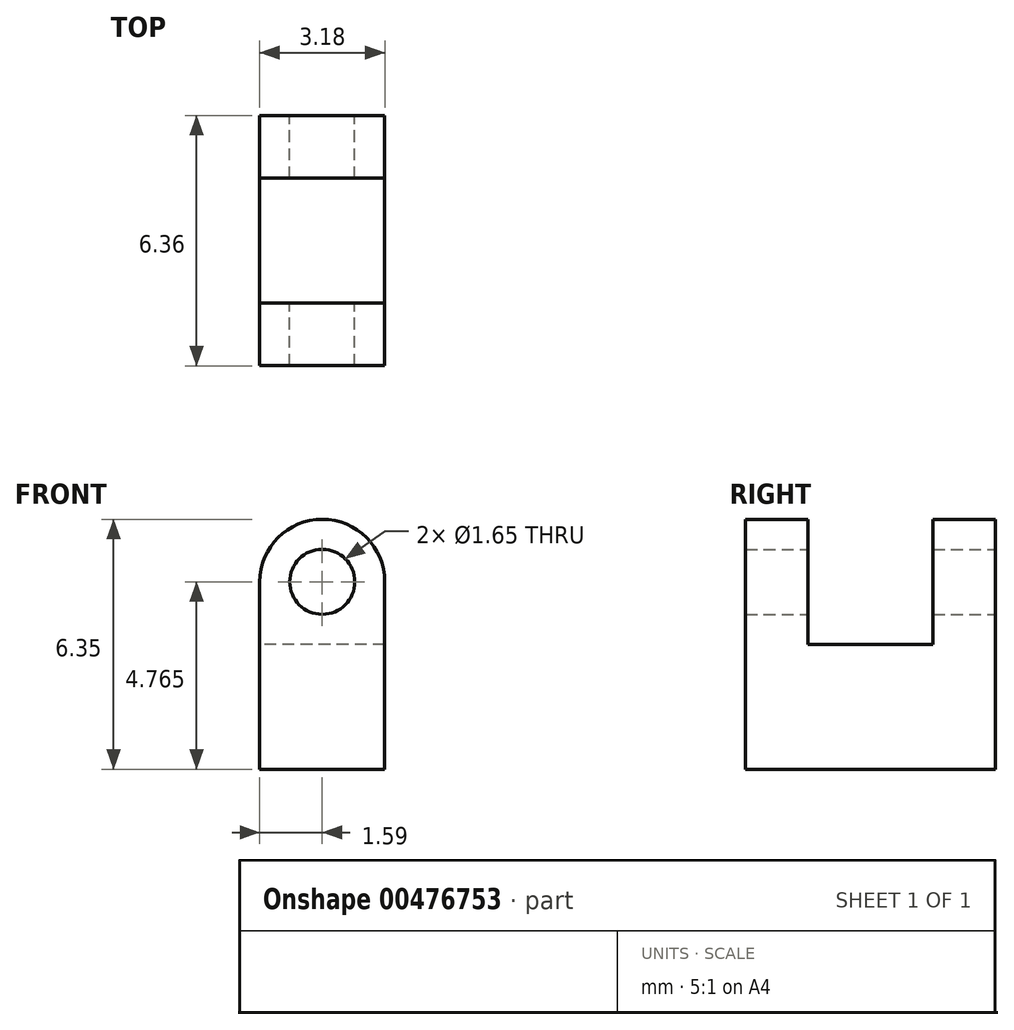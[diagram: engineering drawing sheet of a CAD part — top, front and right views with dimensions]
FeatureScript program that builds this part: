
annotation { "Feature Type Name" : "Feature", "Feature Type Description" : "" }
export const myFeature = defineFeature(function(context is Context, id is Id, definition is map)
    precondition{}
    {
        {
            var Q0;
            Q0=qCreatedBy(makeId("Front.planeOp"),FACE);
            var sketch = newSketch(context, id + "F0", { "sketchPlane" : qUnion([Q0])});
            skLineSegment(sketch, "E0.bottom", {"start": v(1.59, -1.59) * mm, "end": v(-1.59, -1.59) * mm});
            skLineSegment(sketch, "E0.top", {"start": v(1.59, 1.59) * mm, "end": v(-1.59, 1.59) * mm});
            skLineSegment(sketch, "E0.left", {"start": v(1.59, -1.59) * mm, "end": v(1.59, 1.59) * mm});
            skLineSegment(sketch, "E0.right", {"start": v(-1.59, -1.59) * mm, "end": v(-1.59, 1.59) * mm});
            skPoint(sketch, "E0.middle", {"position": v(0, 0) * mm});
            skCircle(sketch, "E1", {"center": v(0, 3.17) * mm, "radius": 1.59 * mm});
            skLineSegment(sketch, "E2", {"start": v(-1.59, 1.59) * mm, "end": v(-1.59, 3.17) * mm});
            skLineSegment(sketch, "E3", {"start": v(1.59, 1.59) * mm, "end": v(1.59, 3.17) * mm});
            skCircle(sketch, "E4.0", {"center": v(0, 3.17) * mm, "radius": 0.83 * mm});
            skLineSegment(sketch, "E5.bottom", {"start": v(2.54, 4.76) * mm, "end": v(-2.54, 4.76) * mm});
            skLineSegment(sketch, "E5.top", {"start": v(2.54, 1.59) * mm, "end": v(-2.54, 1.59) * mm});
            skLineSegment(sketch, "E5.left", {"start": v(2.54, 4.76) * mm, "end": v(2.54, 1.59) * mm});
            skLineSegment(sketch, "E5.right", {"start": v(-2.54, 4.76) * mm, "end": v(-2.54, 1.59) * mm});
            skSolve(sketch);
        }
        {
            var Q0;
            Q0=makeQuery(id+"F0.imprint","IMPRINT",FACE,{"disambiguationData":[TD([[makeQuery(id+"F0.imprint","IMPRINT",EDGE,{"derivedFrom":sQuery(id+"F0.wireOp",EDGE,"E0.bottom")}),-1.0]])]});
            var Q1;
            Q1=makeQuery(id+"F0.imprint","IMPRINT",FACE,{"disambiguationData":[TD([[makeQuery(id+"F0.imprint","IMPRINT",EDGE,{"derivedFrom":sQuery(id+"F0.wireOp",EDGE,"E4.0")}),-1.0]])]});
            var Q2;
            {var subQ0=sQuery(id+"F0.wireOp",EDGE,"E3");Q2=makeQuery(id+"F0.imprint","IMPRINT",FACE,{"disambiguationData":[TD([[makeQuery(id+"F0.imprint","IMPRINT",EDGE,{"derivedFrom":subQ0}),1.0]])]});}
            var Q3;
            {var subQ0=sQuery(id+"F0.wireOp",EDGE,"E2");Q3=makeQuery(id+"F0.imprint","IMPRINT",FACE,{"disambiguationData":[TD([[makeQuery(id+"F0.imprint","IMPRINT",EDGE,{"derivedFrom":subQ0}),-1.0]])]});}
            extrude(context, id + "F1", {"entities" : qUnion([Q0, Q1, Q2, Q3]), "depth" : 6.35 * mm, "symmetric" : true});
        }
        {
            var Q0;
            {var subQ1=sQuery(id+"F0.wireOp",EDGE,"E2");Q0=makeQuery(id+"F0.imprint","IMPRINT",FACE,{"disambiguationData":[TD([[makeQuery(id+"F0.imprint","IMPRINT",EDGE,{"derivedFrom":subQ1}),1.0]])]});}
            var Q1;
            {var subQ0=sQuery(id+"F0.wireOp",EDGE,"E2");Q1=makeQuery(id+"F0.imprint","IMPRINT",FACE,{"disambiguationData":[TD([[makeQuery(id+"F0.imprint","IMPRINT",EDGE,{"derivedFrom":subQ0}),-1.0]])]});}
            var Q2;
            Q2=makeQuery(id+"F0.imprint","IMPRINT",FACE,{"disambiguationData":[TD([[makeQuery(id+"F0.imprint","IMPRINT",EDGE,{"derivedFrom":sQuery(id+"F0.wireOp",EDGE,"E4.0")}),-1.0]])]});
            var Q3;
            Q3=makeQuery(id+"F0.imprint","IMPRINT",FACE,{"disambiguationData":[TD([[makeQuery(id+"F0.imprint","IMPRINT",EDGE,{"derivedFrom":sQuery(id+"F0.wireOp",EDGE,"E4.0")}),1.0]])]});
            var Q4;
            {var subQ0=sQuery(id+"F0.wireOp",EDGE,"E3");Q4=makeQuery(id+"F0.imprint","IMPRINT",FACE,{"disambiguationData":[TD([[makeQuery(id+"F0.imprint","IMPRINT",EDGE,{"derivedFrom":subQ0}),1.0]])]});}
            extrude(context, id + "F2", {"entities" : qUnion([Q0, Q1, Q2, Q3, Q4]), "operationType" : NewBodyOperationType.REMOVE, "depth" : 3.17 * mm, "symmetric" : true});
        }
    });
